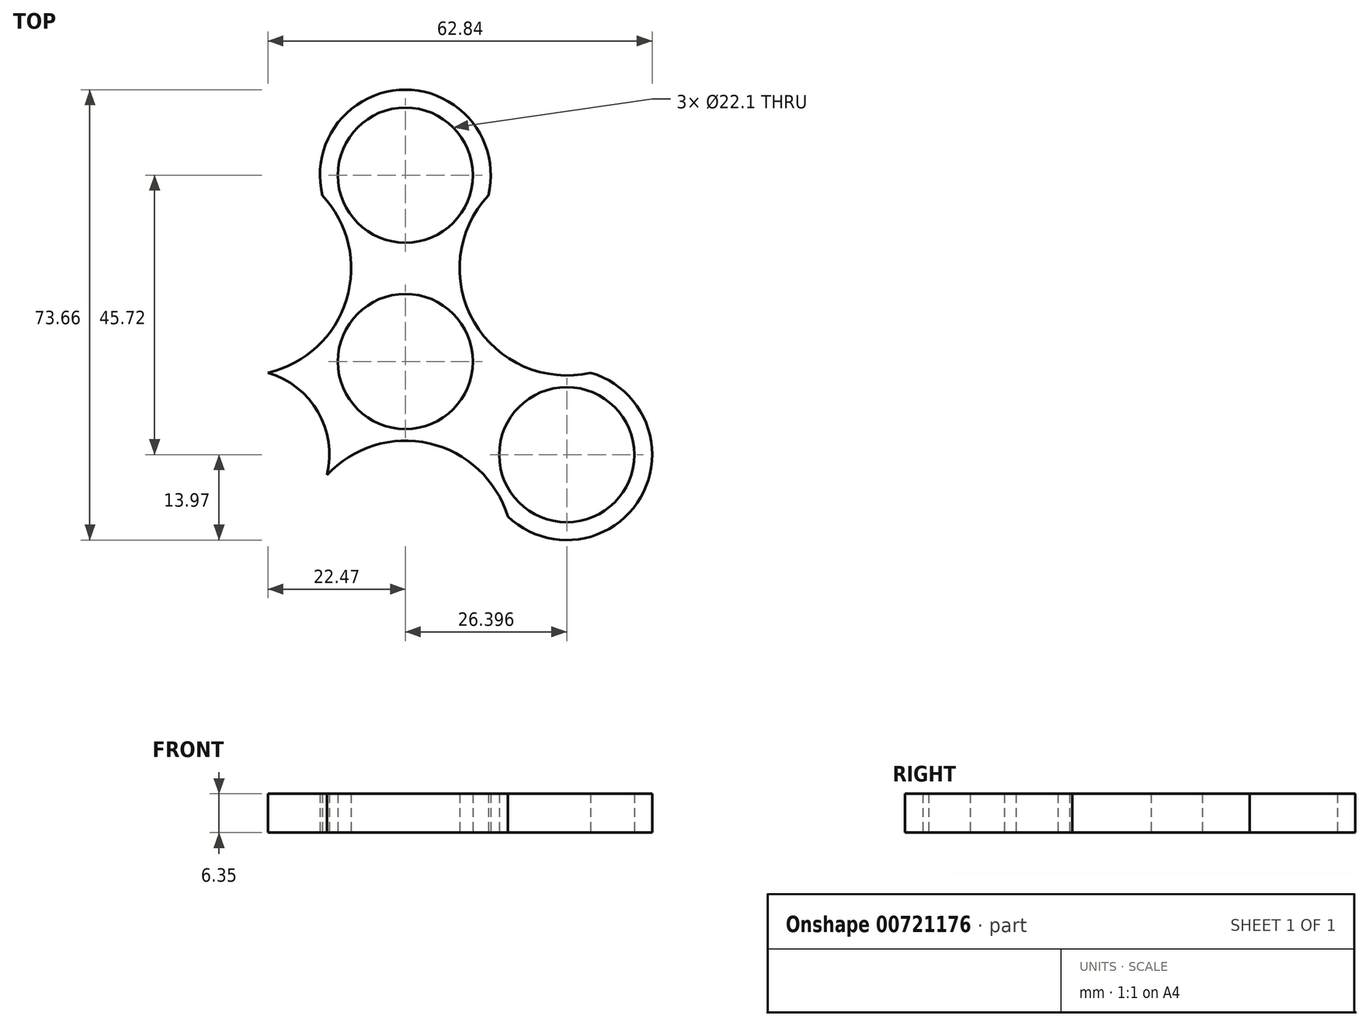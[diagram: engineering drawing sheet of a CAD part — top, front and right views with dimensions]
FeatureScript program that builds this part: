
annotation { "Feature Type Name" : "Feature", "Feature Type Description" : "" }
export const myFeature = defineFeature(function(context is Context, id is Id, definition is map)
    precondition{}
    {
        {
            var Q0;
            Q0=qCreatedBy(makeId("Top.planeOp"),FACE);
            var sketch = newSketch(context, id + "F0", { "sketchPlane" : qUnion([Q0])});
            skCircle(sketch, "E0", {"center": v(0, 0) * mm, "radius": 11.05 * mm});
            skCircle(sketch, "E1", {"center": v(0, 0) * mm, "radius": 13.95 * mm});
            skLineSegment(sketch, "E2", {"start": v(0, 0) * mm, "end": v(0, 30.48) * mm});
            skCircle(sketch, "E3", {"center": v(0, 30.48) * mm, "radius": 11.05 * mm});
            skCircle(sketch, "E4", {"center": v(0, 30.48) * mm, "radius": 13.97 * mm});
            skCircle(sketch, "E5.1.0", {"center": v(-26.4, -15.24) * mm, "radius": 11.05 * mm});
            skCircle(sketch, "E5.2.0", {"center": v(26.4, -15.24) * mm, "radius": 11.05 * mm});
            skCircle(sketch, "E6.1.0", {"center": v(-26.4, -15.24) * mm, "radius": 13.97 * mm});
            skArc(sketch, "E6.2.0", {"start": v(16.75, -25.34) * mm, "mid": v(38.5, -8.26) * mm, "end": v(12.82, -18.54) * mm});
            skArc(sketch, "E7.1.1", {"start": v(13.57, 27.18) * mm, "mid": v(0, 44.45) * mm, "end": v(-13.57, 27.18) * mm});
            skArc(sketch, "E7.2.1", {"start": v(-12.82, -18.54) * mm, "mid": v(-38.5, -8.25) * mm, "end": v(-16.75, -25.34) * mm});
            skLineSegment(sketch, "E8", {"start": v(0, 0) * mm, "end": v(-26.4, 15.24) * mm});
            skArc(sketch, "E9", {"start": v(-30.32, -1.83) * mm, "mid": v(-11.22, 6.48) * mm, "end": v(-13.57, 27.18) * mm});
            skArc(sketch, "E10.1.0", {"start": v(16.75, -25.34) * mm, "mid": v(0, -12.96) * mm, "end": v(-16.75, -25.34) * mm});
            skArc(sketch, "E10.2.0", {"start": v(13.57, 27.18) * mm, "mid": v(11.22, 6.48) * mm, "end": v(30.32, -1.83) * mm});
            skArc(sketch, "E11.trimOffspring", {"start": v(-9.65, 20.38) * mm, "mid": v(0, 16.5) * mm, "end": v(9.65, 20.38) * mm});
            skSolve(sketch);
        }
        {
            var Q0;
            {var subQ0=sQuery(id+"F0.wireOp",EDGE,"E9");var subQ1=sQuery(id+"F0.wireOp",EDGE,"E1");var subQ2=makeQuery(id+"F0.imprint","INTERSECT",VERTEX,{"disambiguationData":[OD(0.0)],"derivedFrom":[subQ1,subQ0]});Q0=makeQuery(id+"F0.imprint","IMPRINT",FACE,{"disambiguationData":[TD([[makeQuery(id+"F0.imprint","IMPRINT",EDGE,{"disambiguationData":[TD([[subQ2,1.0]])],"derivedFrom":subQ1}),-1.0]])]});}
            var Q1;
            {var subQ0=sQuery(id+"F0.wireOp",EDGE,"E10.2.0");var subQ1=sQuery(id+"F0.wireOp",EDGE,"E1");var subQ2=makeQuery(id+"F0.imprint","INTERSECT",VERTEX,{"disambiguationData":[OD(0.0)],"derivedFrom":[subQ1,subQ0]});Q1=makeQuery(id+"F0.imprint","IMPRINT",FACE,{"disambiguationData":[TD([[makeQuery(id+"F0.imprint","IMPRINT",EDGE,{"disambiguationData":[TD([[subQ2,-1.0]])],"derivedFrom":subQ1}),-1.0]])]});}
            var Q2;
            {var subQ0=sQuery(id+"F0.wireOp",EDGE,"E9");var subQ1=sQuery(id+"F0.wireOp",EDGE,"E1");var subQ2=makeQuery(id+"F0.imprint","INTERSECT",VERTEX,{"disambiguationData":[OD(1.0)],"derivedFrom":[subQ1,subQ0]});Q2=makeQuery(id+"F0.imprint","IMPRINT",FACE,{"disambiguationData":[TD([[makeQuery(id+"F0.imprint","IMPRINT",EDGE,{"disambiguationData":[TD([[subQ2,-1.0]])],"derivedFrom":subQ1}),-1.0]])]});}
            var Q3;
            {var subQ0=sQuery(id+"F0.wireOp",EDGE,"E10.2.0");var subQ1=sQuery(id+"F0.wireOp",EDGE,"E1");var subQ2=makeQuery(id+"F0.imprint","INTERSECT",VERTEX,{"disambiguationData":[OD(1.0)],"derivedFrom":[subQ1,subQ0]});Q3=makeQuery(id+"F0.imprint","IMPRINT",FACE,{"disambiguationData":[TD([[makeQuery(id+"F0.imprint","IMPRINT",EDGE,{"disambiguationData":[TD([[subQ2,1.0]])],"derivedFrom":subQ1}),-1.0]])]});}
            var Q4;
            Q4=makeQuery(id+"F0.imprint","IMPRINT",FACE,{"disambiguationData":[TD([[makeQuery(id+"F0.imprint","IMPRINT",EDGE,{"derivedFrom":sQuery(id+"F0.wireOp",EDGE,"E5.2.0")}),-1.0]])]});
            var Q5;
            Q5=makeQuery(id+"F0.imprint","IMPRINT",FACE,{"disambiguationData":[TD([[makeQuery(id+"F0.imprint","IMPRINT",EDGE,{"derivedFrom":sQuery(id+"F0.wireOp",EDGE,"E5.1.0")}),-1.0]])]});
            var Q6;
            Q6=makeQuery(id+"F0.imprint","IMPRINT",FACE,{"disambiguationData":[TD([[makeQuery(id+"F0.imprint","IMPRINT",EDGE,{"derivedFrom":sQuery(id+"F0.wireOp",EDGE,"E3")}),-1.0]])]});
            var Q7;
            {var subQ9=sQuery(id+"F0.wireOp",EDGE,"E0");var subQ13=sQuery(id+"F0.wireOp",EDGE,"E2");var subQ15=makeQuery(id+"F0.imprint","INTERSECT",VERTEX,{"derivedFrom":[subQ9,subQ13]});Q7=makeQuery(id+"F0.imprint","IMPRINT",FACE,{"disambiguationData":[TD([[makeQuery(id+"F0.imprint","IMPRINT",EDGE,{"disambiguationData":[TD([[subQ15,1.0]])],"derivedFrom":subQ9}),-1.0]])]});}
            var Q8;
            {var subQ0=sQuery(id+"F0.wireOp",EDGE,"E2");var subQ1=sQuery(id+"F0.wireOp",EDGE,"E0");var subQ2=makeQuery(id+"F0.imprint","INTERSECT",VERTEX,{"derivedFrom":[subQ1,subQ0]});Q8=makeQuery(id+"F0.imprint","IMPRINT",FACE,{"disambiguationData":[TD([[makeQuery(id+"F0.imprint","IMPRINT",EDGE,{"disambiguationData":[TD([[subQ2,-1.0]])],"derivedFrom":subQ1}),-1.0]])]});}
            extrude(context, id + "F1", {"entities" : qUnion([Q0, Q1, Q2, Q3, Q4, Q5, Q6, Q7, Q8]), "depth" : 6.35 * mm, "offsetDistance" : 25.4 * mm});
        }
    });
